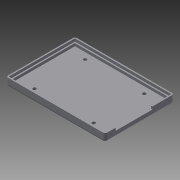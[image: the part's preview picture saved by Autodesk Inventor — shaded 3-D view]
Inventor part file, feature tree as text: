
AUTODESK INVENTOR PART (.ipt)
format: ipt  version: 2015 SP1 (Build 190203100, 203)  size: 151,552 bytes
history: native  units: in
note: dims shown in document units (in); Inventor stores cm internally (conversion verified against a paired STEP export)
features: sketch x5, extrude x4, fillet x1, hole x1
ambient origin geometry x8: Origin, YZ Plane, XZ Plane, XY Plane, X Axis, Y Axis, Z Axis, Center Point
bodies: Solid1 (feature_tree)
feature tree (11):
  extrude  "Extrusion1"  Depth=3.622in
  extrude  "Extrusion2"  Depth=0.0984in
  fillet  "Fillet1"  Radius=0.0984in
  extrude  "Extrusion3"  Depth=0.0984in
  hole  "Hole1"  [1 undecoded]
  extrude  "Extrusion4"  Depth=0.0492in
  sketch  "Sketch1"  dims[d0=2.5197in d1=3.622in]
  sketch  "Sketch2"  dims[d2=0.2953in d3=0.0in d4=0.0984in d5=0.0984in]
  sketch  "Sketch3"  dims[d6=0.0984in d7=0.0984in]
  sketch  "Sketch4"  dims[d8=0.1969in d9=0.0in d10=0.0787in]
  sketch  "Sketch5"  dims[d11=0.0492in d12=0.0492in d13=0.0492in d14=0.0492in d15=0.0984in d16=0.0in d17=0.0984in d18=0.0984in d19=0.0984in d20=0.0984in d21=0.5512in d22=0.5118in d23=2.126in d24=3.2283in d25=0.1378in d26=0.1378in d27=0.1181in d28=0.2362in d29=0.1575in d30=0.0787in d31=90.0deg d32=0.315in d33=0.8108in d34=0.0in d35=0.315in d36=0.7087in d37=0.0984in d38=0.0984in d39=0.0in]
note: 1 required parameter value undecoded (feature->parameter linkage not recoverable at this tier; creation-order binding heuristic only, values carry confidence <= 0.55)
